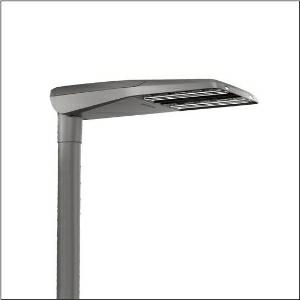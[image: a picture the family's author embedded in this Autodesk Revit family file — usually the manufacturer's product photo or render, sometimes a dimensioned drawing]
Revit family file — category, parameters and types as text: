
# Revit family: streetlight_sl_11_iq_midi___st1_0st0_5_5xc3j51f08me_a600
name_source: partatom
category: Lighting Fixtures
units: mm (PartAtom-declared; Revit-internal decimal feet)

## family parameters
Cut with Voids When Loaded = No
Host = Face
Light Source = No
Part Type = Normal
Room Calculation Point = No
Round Connector Dimension = Use Diameter
Shared = No

## types (1)
- --- (1 x LED, 17650 lm, 124.7 W, 3000K)
    Apparent Load = 125 VA
    CIE Flux Codes = 35 68 96 100 100
    Color Rendering = 70
    Color Temperature = 3000K
    Default Elevation = 1800 mm
    Description = Streetlight SL 11 iQ midi, mast luminaire, primary light control with 3 zone facetted reflector, of plastic, silver coated, highly specular, primary optical cover: cover, of PMMA, transparent, light distribution: ST1.0ST0.5, light emission: direct distribution, primary light characteristic: asymmetric, installation type: post-top, side-entry, lamps: LED, High Power LED, rated values: 17.650lm | 124,7W | 141,5lm/W (begin service life); end service life: 17.650lm | 132,2W; at 50% lumin. flux: 8.825lm | 57,2W | 154,3lm/W, colour temperature: 3000K, colour rendering: CRI > 70, light colour: 730, light setting 1 begin service life: 100% | 17.650lm | 124,7W | 141,5lm/W | 3.000K, light setting 1 end service life: 132,2W, further light settings possible, control: Street-Remote, Auto-Match, Temp-Guard, Lumen-Switch, Night-Set, Smart-Wire, Light-Fading, Desk-Remote (wireless, voltage-free reading and setting of iQ features in the workshop via application-optimized NFC function/RFID function), optimised constant luminous flux control (CLO 2.0), with cable H07RN-F 5x 1.5mm², mains connection: 230..240V, AC, 50/60Hz, connection cable pre-assembled, cable length: 12,5m, luminaire housing, of diecast aluminium, powder-coated, Siteco® metallic grey (DB 702S), please order mast flange separately, inclination adjustable without tools: 0°, 5°, 10°, 15° (post-top) | 0°, -5°, -10°, -15° (side-entry), sealing non-destructively replaceable, multi-level sealing system, length: 780mm, width: 376mm, height: 118mm, mast flange for spigot size: 42mm (side-entry): 5XC10008XM4, 60/48mm (side-entry/post-top): 5XC10108XM2, 76/60mm (side-entry/post-top): 5XC10108XM1, equipment: Power, protection rating (complete): IP66, insulation class (complete): insulation class II (safety insulation), certification: CE, ENEC, ENEC+, VDE, impact resistance: IK10, permissible operating ambient temperature for outdoor applications: -25..+50°C, standard-compliant lighting for roads and squares, Environmental Product Declaration (EPD) tested and certified by an independent institute, packaging unit: 1 piece

Light Distribution: ST1.0ST0.5
    Height = 118 mm
    Lamp = 1 x LED
    Lamp Light Flux = 17650 lm
    Lamp Power = 124.7 W
    Lamp count = 1
    Length = 780 mm
    Luminous efficacy = 142 lm/W
    Manufacturer = Siteco
    ModVariant = No
    Model = 5XC3J51F08ME
    Number of Poles = 1
    OnlyDefault = Yes
    Power Factor = 1
    Product Name = Streetlight SL 11 iQ midi | ST1.0ST0.5
    Product group = mast luminaire | pylon top
    ProductGroupID = 6100
    Protection Class = Protection class II
    Protection Degree = IP 66
    RLX_Detail_Level = 1
    RLX_Emergency_Light_Flux = 0 lm
    RLX_Emergency_Type = 0
    RLX_Emergency_Type_DB = No
    RlxData = <blob elided: 70969 chars, md5=377fb4fc>
    Socket = socket
    Standby Power = 0 W
    System Light Flux = 17650 lm
    System Power = 125 W
    Type Comments = factory setting: luminous flux: 100 % | dim-lin: 254 | 557 mA
    Type Image = l_1005960.jpg
    URL = http://relux.com
    VarID = @adj_040808
    Voltage = 0 V
    Weight = 0.00 kg
    Width = 376 mm

## geometry (parser evidence)
native form markers: Blend x4, Sweep x10
no freeform markers — native parametric forms only
